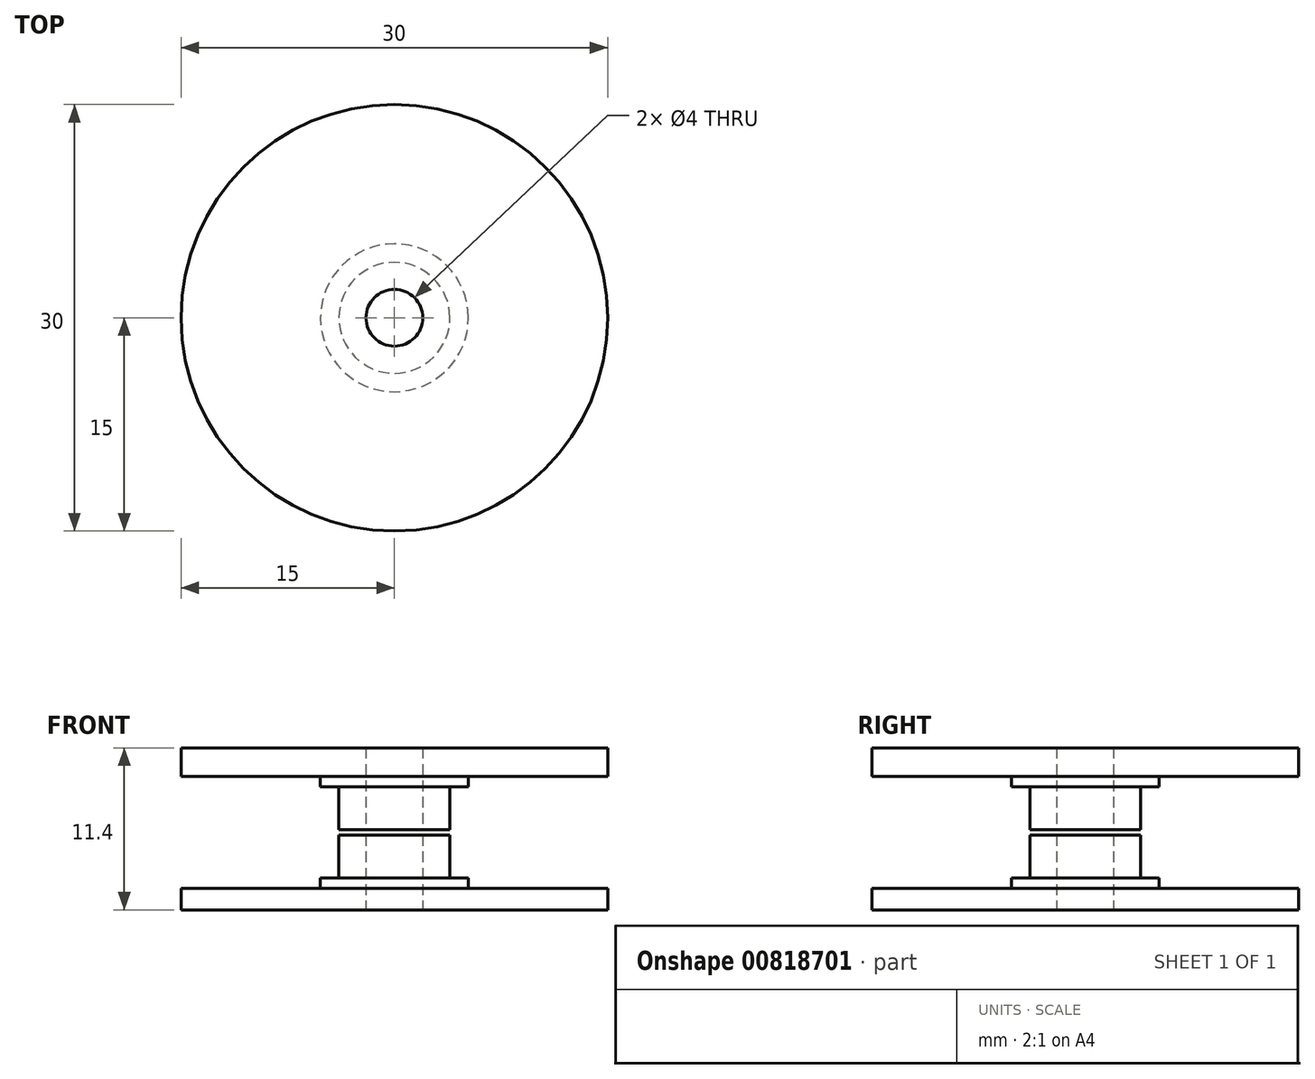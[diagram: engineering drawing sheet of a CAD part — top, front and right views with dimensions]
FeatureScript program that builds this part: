
annotation { "Feature Type Name" : "Feature", "Feature Type Description" : "" }
export const myFeature = defineFeature(function(context is Context, id is Id, definition is map)
    precondition{}
    {
        {
            var Q0;
            Q0=qCreatedBy(makeId("Right.planeOp"),FACE);
            var sketch = newSketch(context, id + "F0", { "sketchPlane" : qUnion([Q0])});
            skLineSegment(sketch, "E0", {"start": v(0, 0) * mm, "end": v(0, 25.62) * mm, "construction": true});
            skLineSegment(sketch, "E1", {"start": v(-2, 0) * mm, "end": v(-15, 0) * mm});
            skLineSegment(sketch, "E2", {"start": v(-15, 0) * mm, "end": v(-15, 1.5) * mm});
            skLineSegment(sketch, "E3", {"start": v(-15, 1.5) * mm, "end": v(-5.2, 1.5) * mm});
            skLineSegment(sketch, "E4", {"start": v(-5.2, 1.5) * mm, "end": v(-5.2, 2.25) * mm});
            skLineSegment(sketch, "E5", {"start": v(-5.2, 2.25) * mm, "end": v(-3.9, 2.25) * mm});
            skLineSegment(sketch, "E6", {"start": v(-3.9, 2.25) * mm, "end": v(-3.9, 5.25) * mm});
            skLineSegment(sketch, "E7", {"start": v(-3.9, 5.25) * mm, "end": v(-2, 5.25) * mm});
            skLineSegment(sketch, "E8", {"start": v(-2, 5.25) * mm, "end": v(-2, 0) * mm});
            skLineSegment(sketch, "E9", {"start": v(-2, 5.65) * mm, "end": v(-3.9, 5.65) * mm});
            skLineSegment(sketch, "E10", {"start": v(-3.9, 5.65) * mm, "end": v(-3.9, 8.65) * mm});
            skLineSegment(sketch, "E11", {"start": v(-3.9, 8.65) * mm, "end": v(-5.2, 8.65) * mm});
            skLineSegment(sketch, "E12", {"start": v(-5.2, 8.65) * mm, "end": v(-5.2, 9.4) * mm});
            skLineSegment(sketch, "E13", {"start": v(-5.2, 9.4) * mm, "end": v(-15, 9.4) * mm});
            skLineSegment(sketch, "E14", {"start": v(-15, 9.4) * mm, "end": v(-15, 9.4) * mm});
            skLineSegment(sketch, "E15", {"start": v(-15, 9.4) * mm, "end": v(-15, 11.4) * mm});
            skLineSegment(sketch, "E16", {"start": v(-15, 11.4) * mm, "end": v(-2, 11.4) * mm});
            skLineSegment(sketch, "E17", {"start": v(-2, 11.4) * mm, "end": v(-2, 5.65) * mm});
            skSolve(sketch);
        }
        {
            var Q0;
            Q0=makeQuery(id+"F0.imprint","IMPRINT",FACE,{"disambiguationData":[TD([[makeQuery(id+"F0.imprint","IMPRINT",EDGE,{"derivedFrom":sQuery(id+"F0.wireOp",EDGE,"E9")}),-1.0]])]});
            var Q1;
            Q1=makeQuery(id+"F0.imprint","IMPRINT",FACE,{"disambiguationData":[TD([[makeQuery(id+"F0.imprint","IMPRINT",EDGE,{"derivedFrom":sQuery(id+"F0.wireOp",EDGE,"E1")}),-1.0]])]});
            var Q2;
            Q2=sQuery(id+"F0.wireOp",EDGE,"E0");
            revolve(context, id + "F1", {"surfaceOperationType" : NewSurfaceOperationType.NEW, "entities" : qUnion([Q0, Q1]), "axis" : qUnion([Q2]), "revolveType" : RevolveType.FULL});
        }
    });
